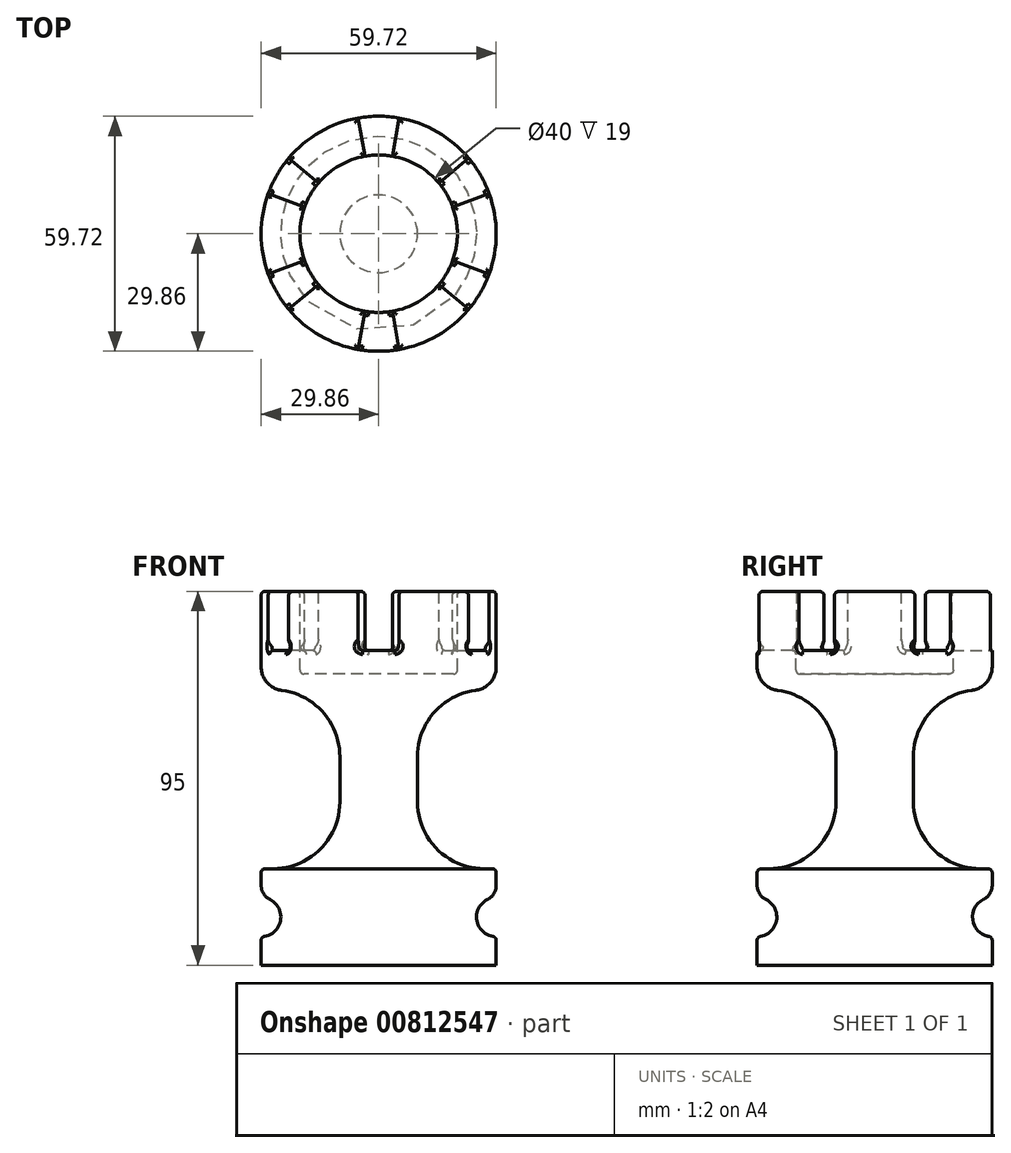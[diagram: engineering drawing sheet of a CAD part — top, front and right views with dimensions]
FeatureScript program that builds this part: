
annotation { "Feature Type Name" : "Feature", "Feature Type Description" : "" }
export const myFeature = defineFeature(function(context is Context, id is Id, definition is map)
    precondition{}
    {
        {
            var Q0;
            Q0=qCreatedBy(makeId("Front.planeOp"),FACE);
            var sketch = newSketch(context, id + "F0", { "sketchPlane" : qUnion([Q0])});
            skLineSegment(sketch, "E0.top", {"start": v(9.86, 24.52) * mm, "end": v(29.86, 24.52) * mm});
            skLineSegment(sketch, "E0.right", {"start": v(29.86, 0) * mm, "end": v(29.86, 7.26) * mm});
            skLineSegment(sketch, "E1.right", {"start": v(9.86, 24.52) * mm, "end": v(9.86, 70) * mm});
            skLineSegment(sketch, "E2.bottom", {"start": v(9.86, 70) * mm, "end": v(29.86, 70) * mm});
            skLineSegment(sketch, "E2.top", {"start": v(0, 95) * mm, "end": v(29.86, 95) * mm});
            skLineSegment(sketch, "E2.right", {"start": v(29.86, 70) * mm, "end": v(29.86, 95) * mm});
            skLineSegment(sketch, "E3", {"start": v(0, 95) * mm, "end": v(0, 0) * mm});
            skLineSegment(sketch, "E4", {"start": v(0, 0) * mm, "end": v(29.86, 0) * mm});
            skArc(sketch, "E5", {"start": v(29.86, 17.26) * mm, "mid": v(24.86, 12.26) * mm, "end": v(29.86, 7.26) * mm});
            skLineSegment(sketch, "E6.trimOffspring", {"start": v(29.86, 17.26) * mm, "end": v(29.86, 24.52) * mm});
            skSolve(sketch);
        }
        {
            var Q0;
            Q0=qSketchRegion(id+"F0",true);
            var Q1;
            Q1=sQuery(id+"F0.wireOp",EDGE,"E3");
            revolve(context, id + "F1", {"surfaceOperationType" : NewSurfaceOperationType.NEW, "entities" : qUnion([Q0]), "axis" : qUnion([Q1]), "revolveType" : RevolveType.FULL});
        }
        {
            var Q0;
            Q0=makeQuery(id+"F1.opRevolve","SWEPT_FACE",FACE,{"disambiguationData":[OSD([sQuery(id+"F0.wireOp",EDGE,"E2.top")])]});
            var sketch = newSketch(context, id + "F2", { "sketchPlane" : qUnion([Q0])});
            skCircle(sketch, "E7", {"center": v(0, 0) * mm, "radius": 20 * mm});
            skSolve(sketch);
        }
        {
            var Q0;
            Q0=qSketchRegion(id+"F2",true);
            extrude(context, id + "F3", {"entities" : qUnion([Q0]), "operationType" : NewBodyOperationType.REMOVE, "oppositeDirection" : true, "depth" : 21 * mm, "offsetDistance" : 25 * mm});
        }
        {
            var Q0;
            Q0=makeQuery(id+"F1.opRevolve","SWEPT_FACE",FACE,{"disambiguationData":[OSD([sQuery(id+"F0.wireOp",EDGE,"E2.top")])]});
            var sketch = newSketch(context, id + "F4", { "sketchPlane" : qUnion([Q0])});
            skLineSegment(sketch, "E8", {"start": v(3.47, 19.7) * mm, "end": v(5.2, 29.54) * mm});
            skLineSegment(sketch, "E9", {"start": v(-3.47, 19.7) * mm, "end": v(-5.2, 29.54) * mm});
            skArc(sketch, "E10", {"start": v(5.2, 29.54) * mm, "mid": v(0, 30) * mm, "end": v(-5.2, 29.54) * mm});
            skArc(sketch, "E11", {"start": v(3.47, 19.7) * mm, "mid": v(0, 20) * mm, "end": v(-3.47, 19.7) * mm});
            skLineSegment(sketch, "E12.1.0", {"start": v(-18.8, 6.84) * mm, "end": v(-28.2, 10.26) * mm});
            skArc(sketch, "E12.1.1", {"start": v(-15.32, 12.86) * mm, "mid": v(-17.32, 10) * mm, "end": v(-18.8, 6.84) * mm});
            skLineSegment(sketch, "E12.1.2", {"start": v(-15.32, 12.86) * mm, "end": v(-22.98, 19.28) * mm});
            skArc(sketch, "E12.1.3", {"start": v(-22.98, 19.28) * mm, "mid": v(-25.98, 15) * mm, "end": v(-28.2, 10.26) * mm});
            skLineSegment(sketch, "E12.2.0", {"start": v(-15.32, -12.86) * mm, "end": v(-22.98, -19.28) * mm});
            skArc(sketch, "E12.2.1", {"start": v(-18.8, -6.84) * mm, "mid": v(-17.32, -10) * mm, "end": v(-15.32, -12.86) * mm});
            skLineSegment(sketch, "E12.2.2", {"start": v(-18.8, -6.84) * mm, "end": v(-28.2, -10.26) * mm});
            skArc(sketch, "E12.2.3", {"start": v(-28.2, -10.26) * mm, "mid": v(-25.98, -15) * mm, "end": v(-22.98, -19.28) * mm});
            skLineSegment(sketch, "E12.3.0", {"start": v(3.47, -19.7) * mm, "end": v(5.2, -29.54) * mm});
            skArc(sketch, "E12.3.1", {"start": v(-3.47, -19.7) * mm, "mid": v(0, -20) * mm, "end": v(3.47, -19.7) * mm});
            skLineSegment(sketch, "E12.3.2", {"start": v(-3.47, -19.7) * mm, "end": v(-5.2, -29.54) * mm});
            skArc(sketch, "E12.3.3", {"start": v(-5.2, -29.54) * mm, "mid": v(0, -30) * mm, "end": v(5.2, -29.54) * mm});
            skLineSegment(sketch, "E12.4.0", {"start": v(18.8, -6.84) * mm, "end": v(28.2, -10.26) * mm});
            skArc(sketch, "E12.4.1", {"start": v(15.32, -12.86) * mm, "mid": v(17.32, -10) * mm, "end": v(18.8, -6.84) * mm});
            skLineSegment(sketch, "E12.4.2", {"start": v(15.32, -12.86) * mm, "end": v(22.98, -19.28) * mm});
            skArc(sketch, "E12.4.3", {"start": v(22.98, -19.28) * mm, "mid": v(25.98, -15) * mm, "end": v(28.2, -10.26) * mm});
            skLineSegment(sketch, "E12.5.0", {"start": v(15.32, 12.86) * mm, "end": v(22.98, 19.28) * mm});
            skArc(sketch, "E12.5.1", {"start": v(18.8, 6.84) * mm, "mid": v(17.32, 10) * mm, "end": v(15.32, 12.86) * mm});
            skLineSegment(sketch, "E12.5.2", {"start": v(18.8, 6.84) * mm, "end": v(28.2, 10.26) * mm});
            skArc(sketch, "E12.5.3", {"start": v(28.2, 10.26) * mm, "mid": v(25.98, 15) * mm, "end": v(22.98, 19.28) * mm});
            skSolve(sketch);
        }
        {
            var Q0;
            Q0=qSketchRegion(id+"F4",true);
            extrude(context, id + "F5", {"entities" : qUnion([Q0]), "operationType" : NewBodyOperationType.REMOVE, "oppositeDirection" : true, "depth" : 15 * mm, "offsetDistance" : 25 * mm});
        }
        {
            var Q0;
            Q0=makeQuery(id+"F1.opRevolve","SWEPT_FACE",FACE,{"disambiguationData":[OSD([sQuery(id+"F0.wireOp",EDGE,"E1.right")])]});
            fillet(context, id + "F6", {"entities" : qUnion([Q0]), "radius" : 17 * mm, "tangentPropagation" : true, "allowEdgeOverflow" : false});
        }
        {
            var Q0;
            Q0=makeQuery(id+"F1.opRevolve","SWEPT_EDGE",EDGE,{"disambiguationData":[OSD([sQuery(id+"F0.wireOp",EDGE,"E2.bottom"),sQuery(id+"F0.wireOp",EDGE,"E2.right")])]});
            fillet(context, id + "F7", {"entities" : qUnion([Q0]), "radius" : 6 * mm, "tangentPropagation" : true, "allowEdgeOverflow" : false});
        }
        {
            var Q0;
            Q0=makeQuery(id+"F1.opRevolve","SWEPT_EDGE",EDGE,{"disambiguationData":[OSD([sQuery(id+"F0.wireOp",EDGE,"E0.top"),sQuery(id+"F0.wireOp",EDGE,"E6.trimOffspring")])]});
            var Q1;
            Q1=makeQuery(id+"F5.boolean.opBoolean","SPLIT",FACE,{"disambiguationData":[TD([makeQuery(id+"F5.opExtrude","SWEPT_FACE",FACE,{"disambiguationData":[OSD([sQuery(id+"F4.wireOp",EDGE,"E12.3.0")])]})])],"derivedFrom":makeQuery(id+"F1.opRevolve","SWEPT_FACE",FACE,{"disambiguationData":[OSD([sQuery(id+"F0.wireOp",EDGE,"E2.top")])]})});
            var Q2;
            Q2=makeQuery(id+"F5.boolean.opBoolean","SPLIT",FACE,{"disambiguationData":[TD([makeQuery(id+"F5.opExtrude","SWEPT_FACE",FACE,{"disambiguationData":[OSD([sQuery(id+"F4.wireOp",EDGE,"E12.4.0")])]})])],"derivedFrom":makeQuery(id+"F1.opRevolve","SWEPT_FACE",FACE,{"disambiguationData":[OSD([sQuery(id+"F0.wireOp",EDGE,"E2.top")])]})});
            var Q3;
            Q3=makeQuery(id+"F5.boolean.opBoolean","SPLIT",FACE,{"disambiguationData":[TD([makeQuery(id+"F5.opExtrude","SWEPT_FACE",FACE,{"disambiguationData":[OSD([sQuery(id+"F4.wireOp",EDGE,"E8")])]})])],"derivedFrom":makeQuery(id+"F1.opRevolve","SWEPT_FACE",FACE,{"disambiguationData":[OSD([sQuery(id+"F0.wireOp",EDGE,"E2.top")])]})});
            var Q4;
            Q4=makeQuery(id+"F5.boolean.opBoolean","SPLIT",FACE,{"disambiguationData":[TD([makeQuery(id+"F5.opExtrude","SWEPT_FACE",FACE,{"disambiguationData":[OSD([sQuery(id+"F4.wireOp",EDGE,"E9")])]})])],"derivedFrom":makeQuery(id+"F1.opRevolve","SWEPT_FACE",FACE,{"disambiguationData":[OSD([sQuery(id+"F0.wireOp",EDGE,"E2.top")])]})});
            var Q5;
            Q5=makeQuery(id+"F5.boolean.opBoolean","SPLIT",FACE,{"disambiguationData":[TD([makeQuery(id+"F5.opExtrude","SWEPT_FACE",FACE,{"disambiguationData":[OSD([sQuery(id+"F4.wireOp",EDGE,"E12.1.0")])]})])],"derivedFrom":makeQuery(id+"F1.opRevolve","SWEPT_FACE",FACE,{"disambiguationData":[OSD([sQuery(id+"F0.wireOp",EDGE,"E2.top")])]})});
            var Q6;
            Q6=makeQuery(id+"F5.boolean.opBoolean","SPLIT",FACE,{"disambiguationData":[TD([makeQuery(id+"F5.opExtrude","SWEPT_FACE",FACE,{"disambiguationData":[OSD([sQuery(id+"F4.wireOp",EDGE,"E12.2.0")])]})])],"derivedFrom":makeQuery(id+"F1.opRevolve","SWEPT_FACE",FACE,{"disambiguationData":[OSD([sQuery(id+"F0.wireOp",EDGE,"E2.top")])]})});
            var Q7;
            Q7=makeQuery(id+"F3.boolean.opBoolean","COPY",EDGE,{"derivedFrom":makeQuery(id+"F3.opExtrude","CAP_EDGE",EDGE,{"disambiguationData":[OSD([sQuery(id+"F2.wireOp",EDGE,"E7")])],"isStart":false})});
            var Q8;
            Q8=makeQuery(id+"F5.boolean.opBoolean","COPY",FACE,{"derivedFrom":makeQuery(id+"F5.opExtrude","CAP_FACE",FACE,{"disambiguationData":[OSD([sQuery(id+"F4.wireOp",EDGE,"E12.1.0"),sQuery(id+"F4.wireOp",EDGE,"E12.1.1"),sQuery(id+"F4.wireOp",EDGE,"E12.1.2"),sQuery(id+"F4.wireOp",EDGE,"E12.1.3")])],"isStart":false})});
            var Q9;
            Q9=makeQuery(id+"F5.boolean.opBoolean","COPY",EDGE,{"derivedFrom":makeQuery(id+"F5.opExtrude","CAP_EDGE",EDGE,{"disambiguationData":[OSD([sQuery(id+"F4.wireOp",EDGE,"E11")])],"isStart":false})});
            var Q10;
            Q10=makeQuery(id+"F5.boolean.opBoolean","INTERSECT",EDGE,{"derivedFrom":[makeQuery(id+"F1.opRevolve","SWEPT_FACE",FACE,{"disambiguationData":[OSD([sQuery(id+"F0.wireOp",EDGE,"E2.right")])]}),makeQuery(id+"F5.opExtrude","CAP_FACE",FACE,{"disambiguationData":[OSD([sQuery(id+"F4.wireOp",EDGE,"E12.5.0"),sQuery(id+"F4.wireOp",EDGE,"E12.5.1"),sQuery(id+"F4.wireOp",EDGE,"E12.5.2"),sQuery(id+"F4.wireOp",EDGE,"E12.5.3")])],"isStart":false})]});
            var Q11;
            Q11=makeQuery(id+"F5.boolean.opBoolean","COPY",FACE,{"derivedFrom":makeQuery(id+"F5.opExtrude","CAP_FACE",FACE,{"disambiguationData":[OSD([sQuery(id+"F4.wireOp",EDGE,"E12.4.0"),sQuery(id+"F4.wireOp",EDGE,"E12.4.1"),sQuery(id+"F4.wireOp",EDGE,"E12.4.2"),sQuery(id+"F4.wireOp",EDGE,"E12.4.3")])],"isStart":false})});
            var Q12;
            Q12=makeQuery(id+"F5.boolean.opBoolean","COPY",FACE,{"derivedFrom":makeQuery(id+"F5.opExtrude","CAP_FACE",FACE,{"disambiguationData":[OSD([sQuery(id+"F4.wireOp",EDGE,"E12.3.0"),sQuery(id+"F4.wireOp",EDGE,"E12.3.1"),sQuery(id+"F4.wireOp",EDGE,"E12.3.2"),sQuery(id+"F4.wireOp",EDGE,"E12.3.3")])],"isStart":false})});
            var Q13;
            Q13=makeQuery(id+"F5.boolean.opBoolean","COPY",FACE,{"derivedFrom":makeQuery(id+"F5.opExtrude","CAP_FACE",FACE,{"disambiguationData":[OSD([sQuery(id+"F4.wireOp",EDGE,"E12.2.0"),sQuery(id+"F4.wireOp",EDGE,"E12.2.1"),sQuery(id+"F4.wireOp",EDGE,"E12.2.2"),sQuery(id+"F4.wireOp",EDGE,"E12.2.3")])],"isStart":false})});
            var Q14;
            Q14=makeQuery(id+"F5.boolean.opBoolean","COPY",FACE,{"derivedFrom":makeQuery(id+"F5.opExtrude","CAP_FACE",FACE,{"disambiguationData":[OSD([sQuery(id+"F4.wireOp",EDGE,"E12.5.0"),sQuery(id+"F4.wireOp",EDGE,"E12.5.1"),sQuery(id+"F4.wireOp",EDGE,"E12.5.2"),sQuery(id+"F4.wireOp",EDGE,"E12.5.3")])],"isStart":false})});
            fillet(context, id + "F8", {"entities" : qUnion([Q0, Q1, Q2, Q3, Q4, Q5, Q6, Q7, Q8, Q9, Q10, Q11, Q12, Q13, Q14]), "radius" : 1 * mm, "tangentPropagation" : true, "allowEdgeOverflow" : false});
        }
        {
            var Q0;
            Q0=makeQuery(id+"F1.opRevolve","SWEPT_EDGE",EDGE,{"disambiguationData":[OSD([sQuery(id+"F0.wireOp",EDGE,"E0.right"),sQuery(id+"F0.wireOp",EDGE,"E5")])]});
            fillet(context, id + "F9", {"entities" : qUnion([Q0]), "radius" : 1 * mm, "tangentPropagation" : true, "allowEdgeOverflow" : false});
        }
        {
            var Q0;
            Q0=makeQuery(id+"F1.opRevolve","SWEPT_EDGE",EDGE,{"disambiguationData":[OSD([sQuery(id+"F0.wireOp",EDGE,"E5"),sQuery(id+"F0.wireOp",EDGE,"E6.trimOffspring")])]});
            fillet(context, id + "F10", {"entities" : qUnion([Q0]), "radius" : 4 * mm, "tangentPropagation" : true, "allowEdgeOverflow" : false});
        }
    });
